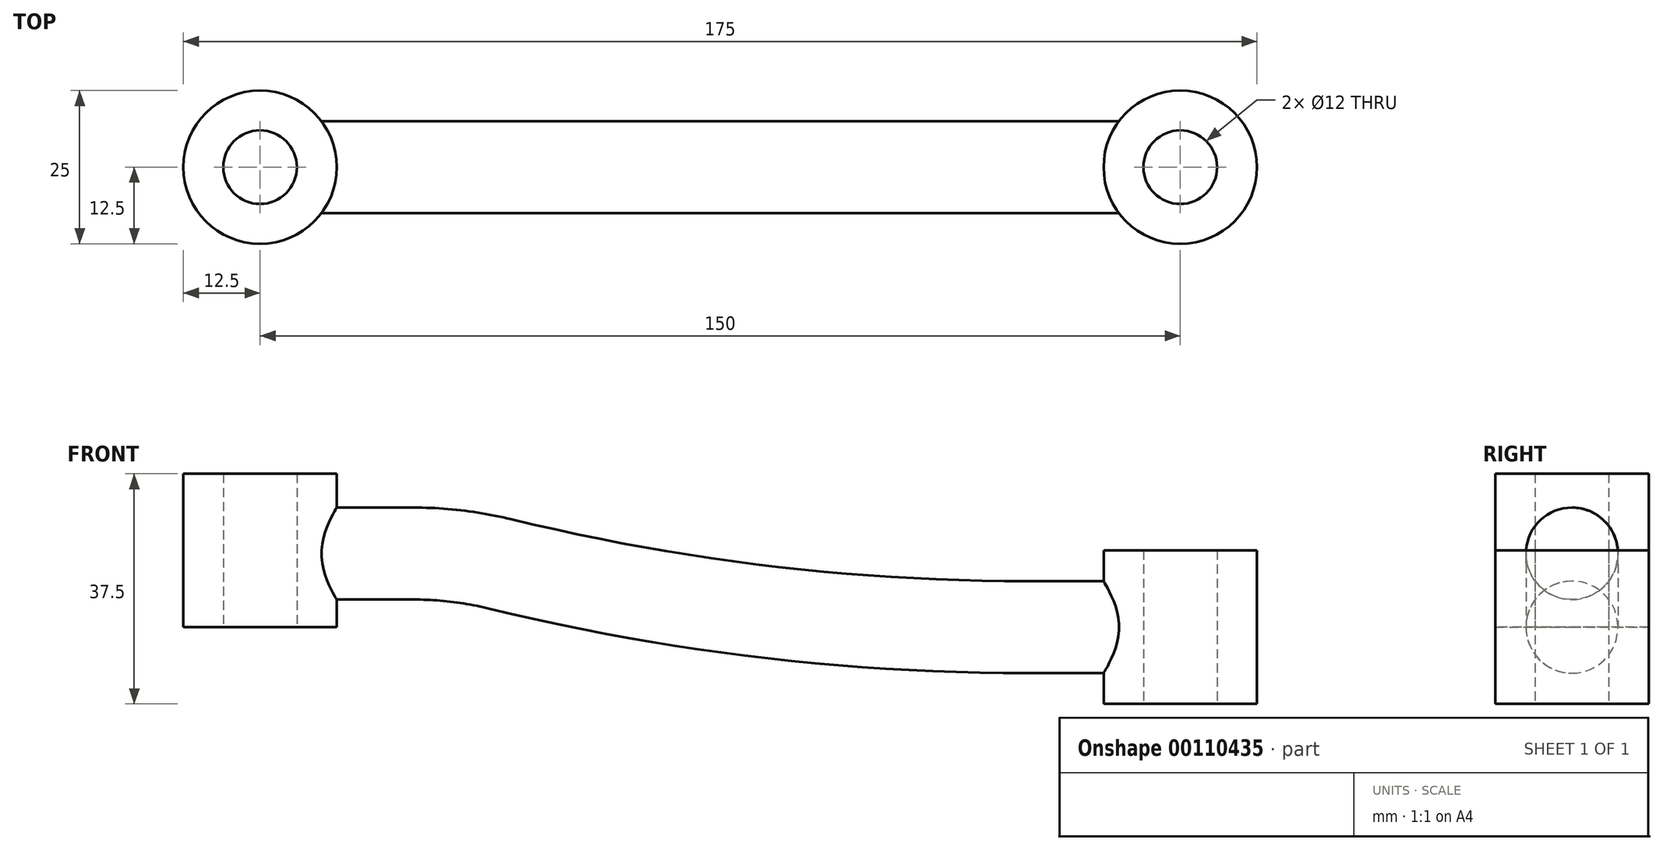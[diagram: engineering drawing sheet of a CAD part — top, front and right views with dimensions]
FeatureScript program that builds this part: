
annotation { "Feature Type Name" : "Feature", "Feature Type Description" : "" }
export const myFeature = defineFeature(function(context is Context, id is Id, definition is map)
    precondition{}
    {
        {
            var Q0;
            Q0=qCreatedBy(makeId("Top.planeOp"),FACE);
            var sketch = newSketch(context, id + "F0", { "sketchPlane" : qUnion([Q0])});
            skCircle(sketch, "E0", {"center": v(0, 0) * mm, "radius": 6 * mm});
            skCircle(sketch, "E1", {"center": v(0, 0) * mm, "radius": 12.5 * mm});
            skCircle(sketch, "E2", {"center": v(150, 0) * mm, "radius": 6 * mm});
            skCircle(sketch, "E3", {"center": v(150, 0) * mm, "radius": 12.5 * mm});
            skSolve(sketch);
        }
        {
            var Q0;
            Q0=makeQuery(id+"F0.imprint","IMPRINT",FACE,{"disambiguationData":[TD([[makeQuery(id+"F0.imprint","IMPRINT",EDGE,{"derivedFrom":sQuery(id+"F0.wireOp",EDGE,"E0")}),-1.0]])]});
            extrude(context, id + "F1", {"entities" : qUnion([Q0]), "depth" : 25 * mm});
        }
        {
            var Q0;
            Q0=makeQuery(id+"F0.imprint","IMPRINT",FACE,{"disambiguationData":[TD([[makeQuery(id+"F0.imprint","IMPRINT",EDGE,{"derivedFrom":sQuery(id+"F0.wireOp",EDGE,"E2")}),-1.0]])]});
            extrude(context, id + "F2", {"entities" : qUnion([Q0]), "endBound" : BoundingType.SYMMETRIC, "depth" : 25 * mm});
        }
        {
            var Q0;
            Q0=qCreatedBy(makeId("Front.planeOp"),FACE);
            var sketch = newSketch(context, id + "F3", { "sketchPlane" : qUnion([Q0])});
            skLineSegment(sketch, "E4", {"start": v(0, 12) * mm, "end": v(25, 12) * mm});
            skLineSegment(sketch, "E5", {"start": v(150, 0) * mm, "end": v(125, 0) * mm});
            skArc(sketch, "E6", {"start": v(25, 12) * mm, "mid": v(32.15, 11.57) * mm, "end": v(39.2, 10.3) * mm});
            skArc(sketch, "E7", {"start": v(39.2, 10.3) * mm, "mid": v(81.79, 2.58) * mm, "end": v(125, 0) * mm});
            skSolve(sketch);
        }
        {
            var Q0;
            Q0=qCreatedBy(makeId("Right.planeOp"),FACE);
            var sketch = newSketch(context, id + "F4", { "sketchPlane" : qUnion([Q0])});
            skCircle(sketch, "E8", {"center": v(0, 12) * mm, "radius": 7.5 * mm});
            skSolve(sketch);
        }
        {
            var Q0;
            Q0 = qSketchRegion(id + "F4", true);
            var Q1;
            Q1 = qConstructionFilter(qBodyType(qCreatedBy(id + "F3" ,EDGE), BodyType.WIRE), ConstructionObject.NO);
            sweep(context, id + "F5", {"operationType" : NewBodyOperationType.ADD, "profiles" : qUnion([Q0]), "path" : qUnion([Q1])});
        }
        {
            var Q0;
            Q0=makeQuery(id+"F1.opExtrude","CAP_FACE",FACE,{"disambiguationData":[OSD([sQuery(id+"F0.wireOp",EDGE,"E0"),sQuery(id+"F0.wireOp",EDGE,"E1")])],"isStart":false});
            var sketch = newSketch(context, id + "F6", { "sketchPlane" : qUnion([Q0])});
            skCircle(sketch, "E9", {"center": v(0, 0) * mm, "radius": 6 * mm});
            skCircle(sketch, "E10", {"center": v(150, 0) * mm, "radius": 6 * mm});
            skSolve(sketch);
        }
        {
            var Q0;
            Q0 = qSketchRegion(id + "F6", true);
            extrude(context, id + "F7", {"entities" : qUnion([Q0]), "operationType" : NewBodyOperationType.REMOVE, "endBound" : BoundingType.THROUGH_ALL, "oppositeDirection" : true, "depth" : 25 * mm});
        }
    });
